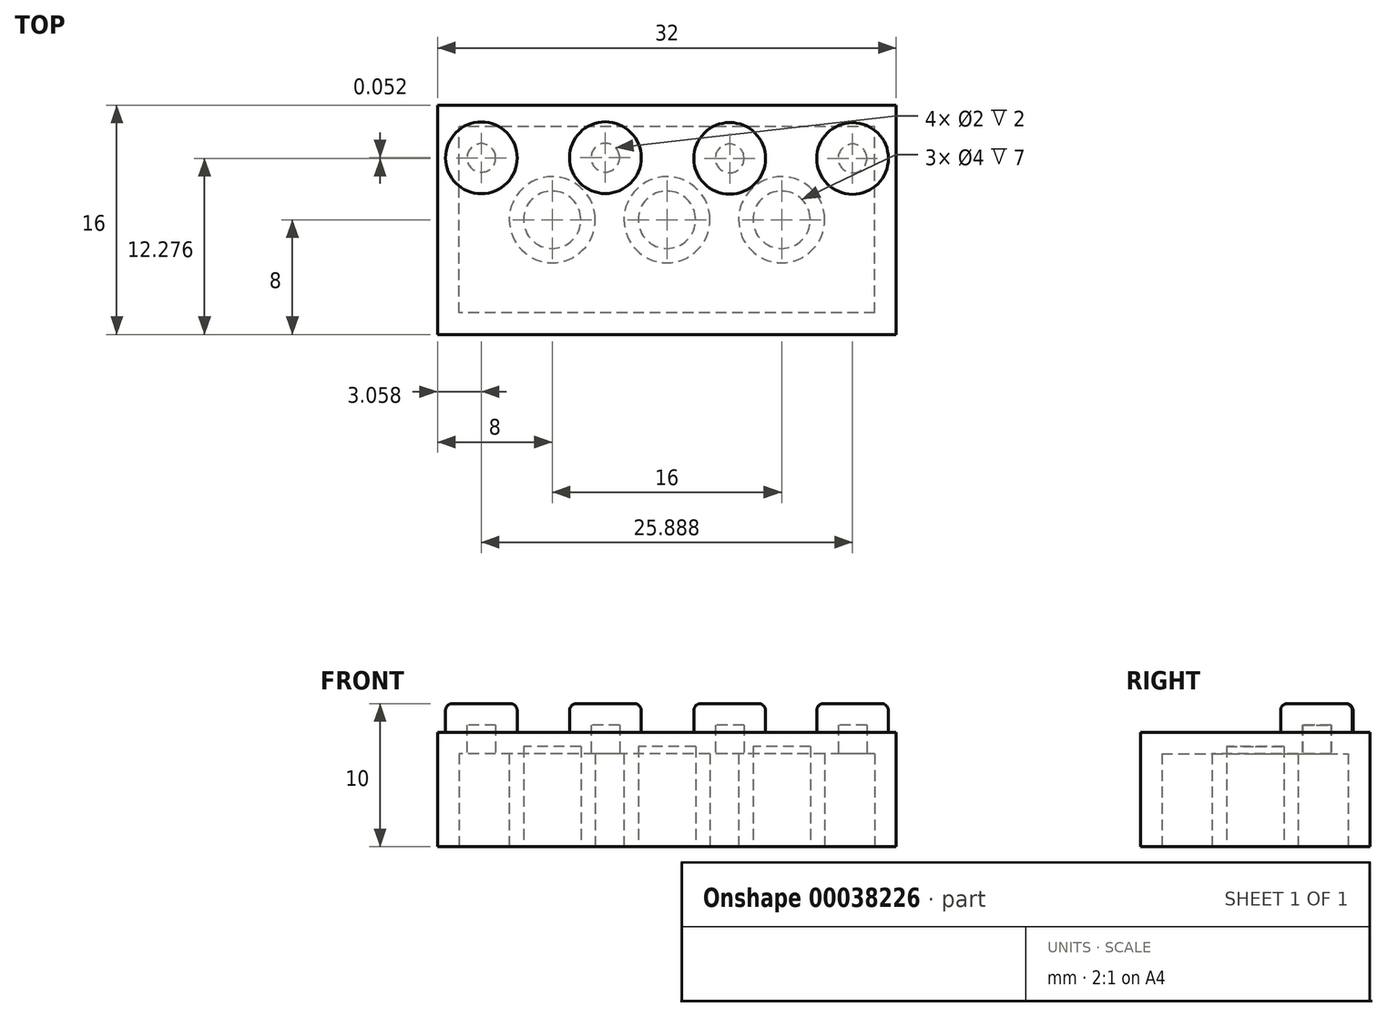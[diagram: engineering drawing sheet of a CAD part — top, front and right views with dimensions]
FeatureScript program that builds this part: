
annotation { "Feature Type Name" : "Feature", "Feature Type Description" : "" }
export const myFeature = defineFeature(function(context is Context, id is Id, definition is map)
    precondition{}
    {
        {
            var Q0;
            Q0=qCreatedBy(makeId("Top.planeOp"),FACE);
            var sketch = newSketch(context, id + "F0", { "sketchPlane" : qUnion([Q0])});
            skLineSegment(sketch, "E0.rect.bottom", {"start": v(16, -8) * mm, "end": v(-16, -8) * mm});
            skLineSegment(sketch, "E0.rect.top", {"start": v(16, 8) * mm, "end": v(-16, 8) * mm});
            skLineSegment(sketch, "E0.rect.left", {"start": v(16, -8) * mm, "end": v(16, 8) * mm});
            skLineSegment(sketch, "E0.rect.right", {"start": v(-16, -8) * mm, "end": v(-16, 8) * mm});
            skPoint(sketch, "E0.rect.middle", {"position": v(0, 0) * mm});
            skSolve(sketch);
        }
        {
            var Q0;
            Q0=makeQuery(id+"F0.imprint","IMPRINT",FACE,{"disambiguationData":[TD([[makeQuery(id+"F0.imprint","IMPRINT",EDGE,{"derivedFrom":sQuery(id+"F0.wireOp",EDGE,"E0.rect.bottom")}),-1.0]])]});
            extrude(context, id + "F1", {"entities" : qUnion([Q0]), "depth" : 8 * mm});
        }
        {
            var Q0;
            Q0=qCreatedBy(makeId("Top.planeOp"),FACE);
            cPlane(context, id + "F2", {"entities" : qUnion([Q0]), "cplaneType" : CPlaneType.OFFSET, "offset" : 8 * mm, "width" : 150 * mm, "height" : 150 * mm});
        }
        {
            var Q0;
            Q0=qCreatedBy(id+"F2.planeOp",FACE);
            var sketch = newSketch(context, id + "F3", { "sketchPlane" : qUnion([Q0])});
            skLineSegment(sketch, "E1.rect.bottom", {"start": v(16, -7.95) * mm, "end": v(-16, -7.95) * mm, "construction": true});
            skLineSegment(sketch, "E1.rect.top", {"start": v(16, 7.95) * mm, "end": v(-16, 7.95) * mm, "construction": true});
            skLineSegment(sketch, "E1.rect.left", {"start": v(16, -7.95) * mm, "end": v(16, 7.95) * mm, "construction": true});
            skLineSegment(sketch, "E1.rect.right", {"start": v(-16, -7.95) * mm, "end": v(-16, 7.95) * mm, "construction": true});
            skPoint(sketch, "E1.rect.middle", {"position": v(0, 0) * mm});
            skLineSegment(sketch, "E2", {"start": v(-16, 7.95) * mm, "end": v(-12.94, 7.95) * mm, "construction": true});
            skLineSegment(sketch, "E3", {"start": v(-12.94, 7.95) * mm, "end": v(-4.31, 7.95) * mm, "construction": true});
            skLineSegment(sketch, "E4", {"start": v(-4.31, 7.95) * mm, "end": v(4.31, 7.95) * mm, "construction": true});
            skLineSegment(sketch, "E5", {"start": v(4.31, 7.95) * mm, "end": v(12.94, 7.95) * mm, "construction": true});
            skLineSegment(sketch, "E6", {"start": v(12.94, 7.95) * mm, "end": v(16, 7.95) * mm, "construction": true});
            skLineSegment(sketch, "E7", {"start": v(16, 7.95) * mm, "end": v(16, 4.31) * mm, "construction": true});
            skLineSegment(sketch, "E8", {"start": v(16, 4.31) * mm, "end": v(16, 0) * mm, "construction": true});
            skLineSegment(sketch, "E9", {"start": v(16, 0) * mm, "end": v(16, -4.31) * mm, "construction": true});
            skLineSegment(sketch, "E10", {"start": v(16, -4.31) * mm, "end": v(16, -7.95) * mm, "construction": true});
            skLineSegment(sketch, "E11", {"start": v(16, 0) * mm, "end": v(-16, 0) * mm, "construction": true});
            skCircle(sketch, "E12", {"center": v(-12.94, 4.31) * mm, "radius": 2.5 * mm});
            skCircle(sketch, "E13", {"center": v(-4.3, 4.33) * mm, "radius": 2.5 * mm});
            skCircle(sketch, "E14", {"center": v(4.38, 4.28) * mm, "radius": 2.5 * mm});
            skCircle(sketch, "E15", {"center": v(12.95, 4.28) * mm, "radius": 2.5 * mm});
            skCircle(sketch, "E16.MirrorC", {"center": v(-4.3, -4.33) * mm, "radius": 2.5 * mm});
            skCircle(sketch, "E17.MirrorC", {"center": v(-12.94, -4.31) * mm, "radius": 2.5 * mm});
            skCircle(sketch, "E18.MirrorC", {"center": v(4.38, -4.28) * mm, "radius": 2.5 * mm});
            skCircle(sketch, "E19.MirrorC", {"center": v(12.95, -4.28) * mm, "radius": 2.5 * mm});
            skSolve(sketch);
        }
        {
            var Q0;
            Q0=makeQuery(id+"F3.imprint","IMPRINT",FACE,{"disambiguationData":[TD([[makeQuery(id+"F3.imprint","IMPRINT",EDGE,{"derivedFrom":sQuery(id+"F3.wireOp",EDGE,"E12")}),1.0]])]});
            var Q1;
            Q1=makeQuery(id+"F3.imprint","IMPRINT",FACE,{"disambiguationData":[TD([[makeQuery(id+"F3.imprint","IMPRINT",EDGE,{"derivedFrom":sQuery(id+"F3.wireOp",EDGE,"E13")}),1.0]])]});
            var Q2;
            Q2=makeQuery(id+"F3.imprint","IMPRINT",FACE,{"disambiguationData":[TD([[makeQuery(id+"F3.imprint","IMPRINT",EDGE,{"derivedFrom":sQuery(id+"F3.wireOp",EDGE,"E14")}),1.0]])]});
            var Q3;
            Q3=makeQuery(id+"F3.imprint","IMPRINT",FACE,{"disambiguationData":[TD([[makeQuery(id+"F3.imprint","IMPRINT",EDGE,{"derivedFrom":sQuery(id+"F3.wireOp",EDGE,"E15")}),1.0]])]});
            var Q4;
            Q4=makeQuery(id+"F3.imprint","IMPRINT",FACE,{"disambiguationData":[TD([[makeQuery(id+"F3.imprint","IMPRINT",EDGE,{"derivedFrom":sQuery(id+"F3.wireOp",EDGE,"E19.MirrorC")}),-1.0]])]});
            var Q5;
            Q5=makeQuery(id+"F3.imprint","IMPRINT",FACE,{"disambiguationData":[TD([[makeQuery(id+"F3.imprint","IMPRINT",EDGE,{"derivedFrom":sQuery(id+"F3.wireOp",EDGE,"E18.MirrorC")}),-1.0]])]});
            var Q6;
            Q6=makeQuery(id+"F3.imprint","IMPRINT",FACE,{"disambiguationData":[TD([[makeQuery(id+"F3.imprint","IMPRINT",EDGE,{"derivedFrom":sQuery(id+"F3.wireOp",EDGE,"E16.MirrorC")}),-1.0]])]});
            var Q7;
            Q7=makeQuery(id+"F3.imprint","IMPRINT",FACE,{"disambiguationData":[TD([[makeQuery(id+"F3.imprint","IMPRINT",EDGE,{"derivedFrom":sQuery(id+"F3.wireOp",EDGE,"E17.MirrorC")}),-1.0]])]});
            extrude(context, id + "F4", {"entities" : qUnion([Q0, Q1, Q2, Q3, Q4, Q5, Q6, Q7]), "operationType" : NewBodyOperationType.ADD, "depth" : 2 * mm});
        }
        {
            var Q0;
            Q0=qCreatedBy(makeId("Top.planeOp"),FACE);
            var sketch = newSketch(context, id + "F5", { "sketchPlane" : qUnion([Q0])});
            skPoint(sketch, "E20.rect.middle", {"position": v(0, 0) * mm});
            skLineSegment(sketch, "E21.rect.bottom", {"start": v(16, 8) * mm, "end": v(-16, 8) * mm, "construction": true});
            skLineSegment(sketch, "E21.rect.top", {"start": v(16, -8) * mm, "end": v(-16, -8) * mm, "construction": true});
            skLineSegment(sketch, "E21.rect.left", {"start": v(16, 8) * mm, "end": v(16, -8) * mm, "construction": true});
            skLineSegment(sketch, "E21.rect.right", {"start": v(-16, 8) * mm, "end": v(-16, -8) * mm, "construction": true});
            skLineSegment(sketch, "E22", {"start": v(-16, -8) * mm, "end": v(-8, -8) * mm, "construction": true});
            skLineSegment(sketch, "E23", {"start": v(-8, -8) * mm, "end": v(0, -8) * mm, "construction": true});
            skLineSegment(sketch, "E24", {"start": v(0, -8) * mm, "end": v(8, -8) * mm, "construction": true});
            skLineSegment(sketch, "E25", {"start": v(8, -8) * mm, "end": v(16, -8) * mm, "construction": true});
            skLineSegment(sketch, "E26", {"start": v(-16, -8) * mm, "end": v(-16, 0) * mm, "construction": true});
            skLineSegment(sketch, "E27", {"start": v(-16, 0) * mm, "end": v(-16, 8) * mm, "construction": true});
            skCircle(sketch, "E28", {"center": v(-8, 0) * mm, "radius": 3 * mm});
            skCircle(sketch, "E29", {"center": v(0, 0) * mm, "radius": 3 * mm});
            skCircle(sketch, "E30", {"center": v(8, 0) * mm, "radius": 3 * mm});
            skSolve(sketch);
        }
        {
            var Q0;
            Q0=makeQuery(id+"F4.opExtrude","CAP_FACE",FACE,{"disambiguationData":[OSD([sQuery(id+"F3.wireOp",EDGE,"E12")])],"isStart":false});
            var Q1;
            Q1=makeQuery(id+"F4.opExtrude","CAP_FACE",FACE,{"disambiguationData":[OSD([sQuery(id+"F3.wireOp",EDGE,"E17.MirrorC")])],"isStart":false});
            var Q2;
            Q2=makeQuery(id+"F4.opExtrude","CAP_FACE",FACE,{"disambiguationData":[OSD([sQuery(id+"F3.wireOp",EDGE,"E16.MirrorC")])],"isStart":false});
            var Q3;
            Q3=makeQuery(id+"F4.opExtrude","CAP_FACE",FACE,{"disambiguationData":[OSD([sQuery(id+"F3.wireOp",EDGE,"E13")])],"isStart":false});
            var Q4;
            Q4=makeQuery(id+"F4.opExtrude","CAP_FACE",FACE,{"disambiguationData":[OSD([sQuery(id+"F3.wireOp",EDGE,"E14")])],"isStart":false});
            var Q5;
            Q5=makeQuery(id+"F4.opExtrude","CAP_FACE",FACE,{"disambiguationData":[OSD([sQuery(id+"F3.wireOp",EDGE,"E18.MirrorC")])],"isStart":false});
            var Q6;
            Q6=makeQuery(id+"F4.opExtrude","CAP_FACE",FACE,{"disambiguationData":[OSD([sQuery(id+"F3.wireOp",EDGE,"E15")])],"isStart":false});
            var Q7;
            Q7=makeQuery(id+"F4.opExtrude","CAP_FACE",FACE,{"disambiguationData":[OSD([sQuery(id+"F3.wireOp",EDGE,"E19.MirrorC")])],"isStart":false});
            fillet(context, id + "F6", {"entities" : qUnion([Q0, Q1, Q2, Q3, Q4, Q5, Q6, Q7]), "radius" : 0.5 * mm, "tangentPropagation" : true, "allowEdgeOverflow" : false});
        }
        {
            var Q0;
            Q0=makeQuery(id+"F1.opExtrude","CAP_FACE",FACE,{"disambiguationData":[OSD([sQuery(id+"F0.wireOp",EDGE,"E0.rect.bottom"),sQuery(id+"F0.wireOp",EDGE,"E0.rect.top"),sQuery(id+"F0.wireOp",EDGE,"E0.rect.left"),sQuery(id+"F0.wireOp",EDGE,"E0.rect.right")])],"isStart":true});
            var Q1;
            Q1=makeQuery(id+"F1.opExtrude","SWEPT_BODY",BODY,{"disambiguationData":[OSD([sQuery(id+"F0.wireOp",EDGE,"E0.rect.bottom"),sQuery(id+"F0.wireOp",EDGE,"E0.rect.top"),sQuery(id+"F0.wireOp",EDGE,"E0.rect.left"),sQuery(id+"F0.wireOp",EDGE,"E0.rect.right")])]});
            shell(context, id + "F7", {"entities" : qUnion([Q0]), "parts" : qUnion([Q1]), "thickness" : 1.5 * mm});
        }
        {
            var Q0;
            Q0 = qSketchRegion(id + "F5", true);
            extrude(context, id + "F8", {"entities" : qUnion([Q0]), "operationType" : NewBodyOperationType.ADD, "depth" : 8 * mm});
        }
        {
            var Q0;
            Q0=makeQuery(id+"F8.opExtrude","CAP_FACE",FACE,{"disambiguationData":[OSD([sQuery(id+"F5.wireOp",EDGE,"E28")])],"isStart":true});
            var Q1;
            Q1=makeQuery(id+"F8.opExtrude","CAP_FACE",FACE,{"disambiguationData":[OSD([sQuery(id+"F5.wireOp",EDGE,"E29")])],"isStart":true});
            var Q2;
            Q2=makeQuery(id+"F8.opExtrude","CAP_FACE",FACE,{"disambiguationData":[OSD([sQuery(id+"F5.wireOp",EDGE,"E30")])],"isStart":true});
            shell(context, id + "F9", {"entities" : qUnion([Q0, Q1, Q2]), "thickness" : 1 * mm});
        }
    });
